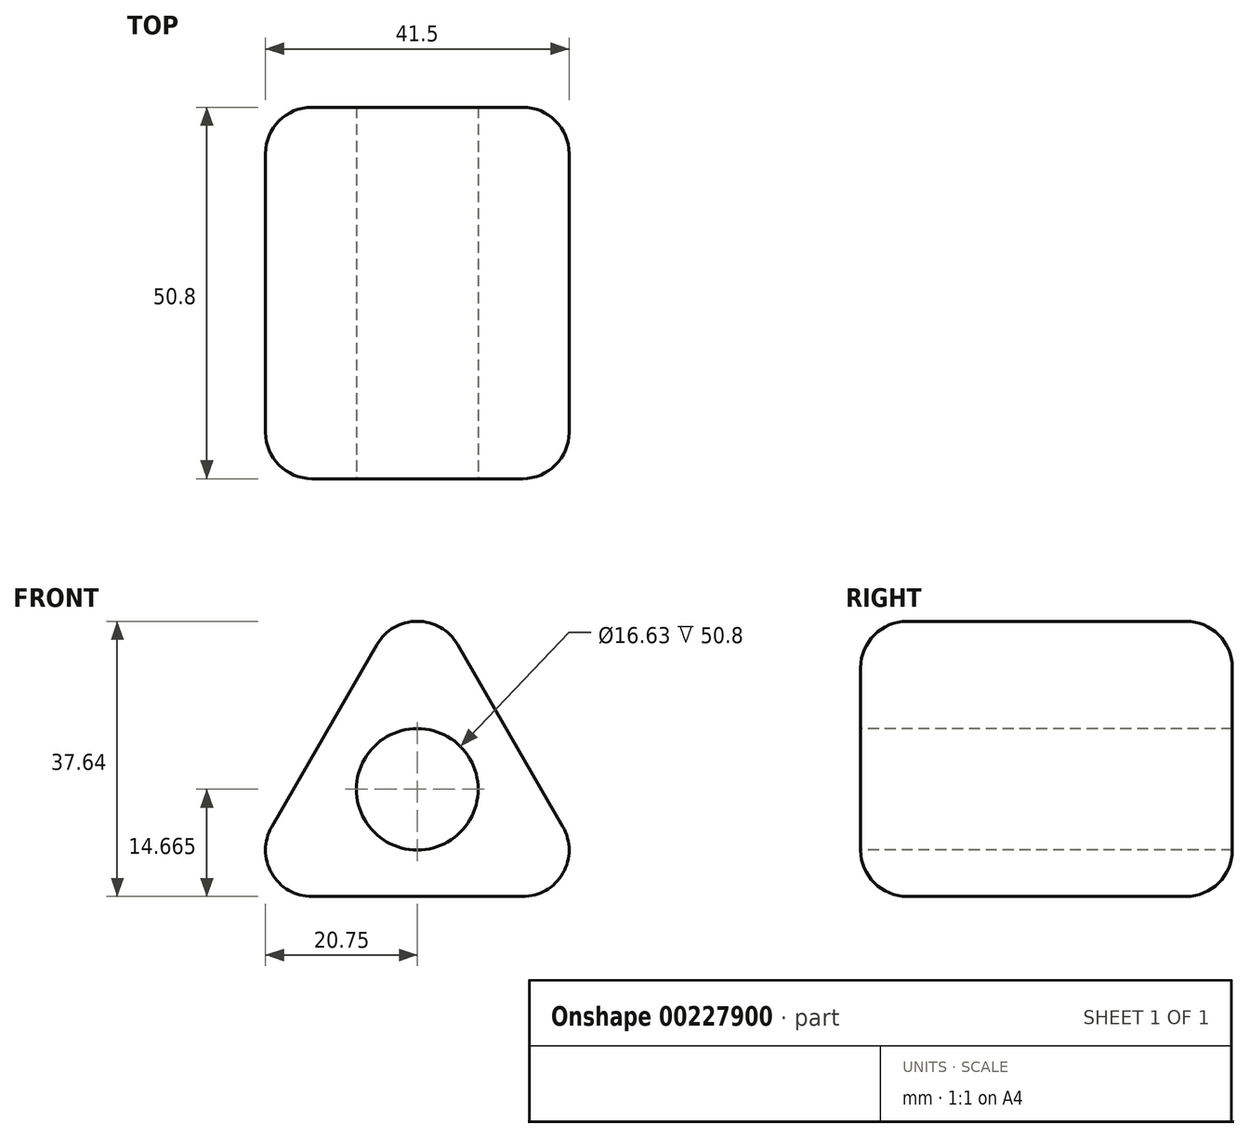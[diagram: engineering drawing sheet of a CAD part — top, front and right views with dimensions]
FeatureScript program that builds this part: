
annotation { "Feature Type Name" : "Feature", "Feature Type Description" : "" }
export const myFeature = defineFeature(function(context is Context, id is Id, definition is map)
    precondition{}
    {
        {
            var Q0;
            Q0=qCreatedBy(makeId("Front.planeOp"),FACE);
            var sketch = newSketch(context, id + "F0", { "sketchPlane" : qUnion([Q0])});
            skLineSegment(sketch, "E0", {"start": v(0, 0) * mm, "end": v(25.4, 0) * mm});
            skLineSegment(sketch, "E1", {"start": v(25.4, 0) * mm, "end": v(-25.4, 0) * mm});
            skLineSegment(sketch, "E2", {"start": v(-25.4, 0) * mm, "end": v(0, 44) * mm});
            skLineSegment(sketch, "E3", {"start": v(25.4, 0) * mm, "end": v(0, 44) * mm});
            skSolve(sketch);
        }
        {
            var Q0;
            {var subQ2=sQuery(id+"F0.wireOp",EDGE,"E2");Q0=makeQuery(id+"F0.imprint","IMPRINT",FACE,{"disambiguationData":[TD([[makeQuery(id+"F0.imprint","IMPRINT",EDGE,{"derivedFrom":subQ2}),-1.0]])]});}
            extrude(context, id + "F1", {"entities" : qUnion([Q0]), "depth" : 50.8 * mm});
        }
        {
            var Q0;
            Q0=makeQuery(id+"F1.opExtrude","SWEPT_EDGE",EDGE,{"disambiguationData":[OSD([sQuery(id+"F0.wireOp",EDGE,"E2"),sQuery(id+"F0.wireOp",EDGE,"E3")])]});
            var Q1;
            Q1=makeQuery(id+"F1.opExtrude","CAP_EDGE",EDGE,{"disambiguationData":[OSD([sQuery(id+"F0.wireOp",EDGE,"E3")])],"isStart":false});
            var Q2;
            Q2=makeQuery(id+"F1.opExtrude","CAP_EDGE",EDGE,{"disambiguationData":[OSD([sQuery(id+"F0.wireOp",EDGE,"E2")])],"isStart":false});
            var Q3;
            Q3=makeQuery(id+"F1.opExtrude","CAP_EDGE",EDGE,{"disambiguationData":[OSD([sQuery(id+"F0.wireOp",EDGE,"E1")])],"isStart":false});
            var Q4;
            Q4=makeQuery(id+"F1.opExtrude","SWEPT_EDGE",EDGE,{"disambiguationData":[OSD([sQuery(id+"F0.wireOp",EDGE,"E1"),sQuery(id+"F0.wireOp",EDGE,"E3")])]});
            var Q5;
            Q5=makeQuery(id+"F1.opExtrude","CAP_EDGE",EDGE,{"disambiguationData":[OSD([sQuery(id+"F0.wireOp",EDGE,"E3")])],"isStart":true});
            var Q6;
            Q6=makeQuery(id+"F1.opExtrude","CAP_EDGE",EDGE,{"disambiguationData":[OSD([sQuery(id+"F0.wireOp",EDGE,"E1")])],"isStart":true});
            var Q7;
            Q7=makeQuery(id+"F1.opExtrude","CAP_EDGE",EDGE,{"disambiguationData":[OSD([sQuery(id+"F0.wireOp",EDGE,"E2")])],"isStart":true});
            var Q8;
            Q8=makeQuery(id+"F1.opExtrude","SWEPT_EDGE",EDGE,{"disambiguationData":[OSD([sQuery(id+"F0.wireOp",EDGE,"E1"),sQuery(id+"F0.wireOp",EDGE,"E2")])]});
            fillet(context, id + "F2", {"entities" : qUnion([Q0, Q1, Q2, Q3, Q4, Q5, Q6, Q7, Q8]), "radius" : 6.35 * mm, "tangentPropagation" : true, "allowEdgeOverflow" : false});
        }
        {
            var Q0;
            Q0=makeQuery(id+"F1.opExtrude","CAP_FACE",FACE,{"disambiguationData":[OSD([sQuery(id+"F0.wireOp",EDGE,"E1"),sQuery(id+"F0.wireOp",EDGE,"E2"),sQuery(id+"F0.wireOp",EDGE,"E3")])],"isStart":false});
            var sketch = newSketch(context, id + "F3", { "sketchPlane" : qUnion([Q0])});
            skCircle(sketch, "E4", {"center": v(0, 14.66) * mm, "radius": 8.31 * mm});
            skSolve(sketch);
        }
        {
            var Q0;
            {var subQ0=sQuery(id+"F3.wireOp",EDGE,"E4");var subQ1=sQuery(id+"F0.wireOp",EDGE,"E3");var subQ2=sQuery(id+"F0.wireOp",EDGE,"E2");var subQ3=sQuery(id+"F0.wireOp",EDGE,"E1");var subQ4=makeQuery(id+"F1.opExtrude","CAP_FACE",FACE,{"disambiguationData":[OSD([subQ3,subQ2,subQ1])],"isStart":false});var subQ5=makeQuery(id+"F3.imprint","INTERSECT",VERTEX,{"derivedFrom":[makeQuery(id+"F2.opFillet","BLEND_EDGE",EDGE,{"blendedFrom":[makeQuery(id+"F1.opExtrude","CAP_EDGE",EDGE,{"disambiguationData":[OSD([subQ2])],"isStart":false}),subQ4],"blendedInto":[subQ4]}),subQ0]});Q0=makeQuery(id+"F3.imprint","IMPRINT",FACE,{"disambiguationData":[TD([[makeQuery(id+"F3.imprint","IMPRINT",EDGE,{"disambiguationData":[TD([[subQ5,1.0]])],"derivedFrom":subQ0}),1.0]])]});}
            extrude(context, id + "F4", {"entities" : qUnion([Q0]), "operationType" : NewBodyOperationType.REMOVE, "oppositeDirection" : true, "depth" : 68.83 * mm, "hasSecondDirection" : true, "secondDirectionBound" : SecondDirectionBoundingType.THROUGH_ALL, "secondDirectionOppositeDirection" : false, "secondDirectionDepth" : 25.4 * mm});
        }
    });
